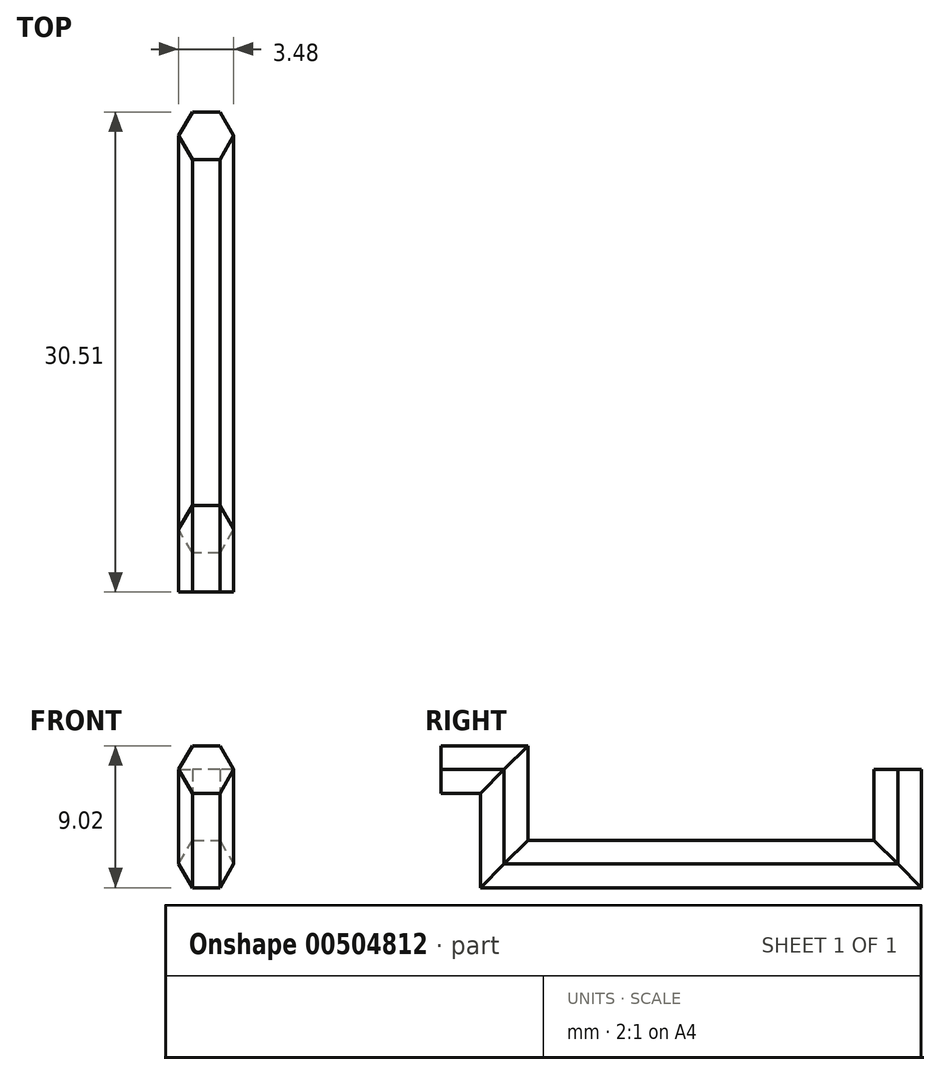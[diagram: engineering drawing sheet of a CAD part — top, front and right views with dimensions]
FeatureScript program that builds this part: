
annotation { "Feature Type Name" : "Feature", "Feature Type Description" : "" }
export const myFeature = defineFeature(function(context is Context, id is Id, definition is map)
    precondition{}
    {
        {
            var Q0;
            Q0=qCreatedBy(makeId("Right.planeOp"),FACE);
            var sketch = newSketch(context, id + "F0", { "sketchPlane" : qUnion([Q0])});
            skLineSegment(sketch, "E0", {"start": v(-12.5, 0) * mm, "end": v(12.5, 0) * mm});
            skLineSegment(sketch, "E1", {"start": v(12.5, 0) * mm, "end": v(12.5, 6) * mm});
            skLineSegment(sketch, "E2", {"start": v(-12.5, 0) * mm, "end": v(-12.5, 6) * mm});
            skLineSegment(sketch, "E3", {"start": v(-12.5, 6) * mm, "end": v(-16.5, 6) * mm});
            skLineSegment(sketch, "E4", {"start": v(-3.5, 0) * mm, "end": v(-3.5, -5) * mm});
            skPoint(sketch, "E5", {"position": v(12.5, 6) * mm});
            skPoint(sketch, "E6", {"position": v(-3.5, -5) * mm});
            skSolve(sketch);
        }
        {
            var Q0;
            Q0=qCreatedBy(makeId("Front.planeOp"),FACE);
            var sketch = newSketch(context, id + "F1", { "sketchPlane" : qUnion([Q0])});
            skCircle(sketch, "E7.cCircle", {"center": v(0, 0) * mm, "radius": 1.51 * mm, "construction": true});
            skLineSegment(sketch, "E7.0", {"start": v(0.87, -1.51) * mm, "end": v(-0.87, -1.51) * mm});
            skLineSegment(sketch, "E7.1", {"start": v(-0.87, -1.51) * mm, "end": v(-1.74, 0) * mm});
            skLineSegment(sketch, "E7.2", {"start": v(-1.74, 0) * mm, "end": v(-0.87, 1.51) * mm});
            skLineSegment(sketch, "E7.3", {"start": v(-0.87, 1.51) * mm, "end": v(0.87, 1.51) * mm});
            skLineSegment(sketch, "E7.4", {"start": v(0.87, 1.51) * mm, "end": v(1.74, 0) * mm});
            skLineSegment(sketch, "E7.5", {"start": v(1.74, 0) * mm, "end": v(0.87, -1.51) * mm});
            skPoint(sketch, "E7.0.midPoint", {"position": v(0, -1.51) * mm});
            skSolve(sketch);
        }
        {
            var Q0;
            Q0=makeQuery(id+"F1.imprint","IMPRINT",FACE,{"disambiguationData":[TD([[makeQuery(id+"F1.imprint","IMPRINT",EDGE,{"derivedFrom":sQuery(id+"F1.wireOp",EDGE,"E7.0")}),-1.0]])]});
            var Q1;
            Q1=sQuery(id+"F0.wireOp",EDGE,"E0");
            var Q2;
            Q2=sQuery(id+"F0.wireOp",EDGE,"E2");
            var Q3;
            Q3=sQuery(id+"F0.wireOp",EDGE,"E3");
            sweep(context, id + "F2", {"profiles" : qUnion([Q0]), "path" : qUnion([Q1, Q2, Q3])});
        }
        {
            var Q0;
            Q0=makeQuery(id+"F1.imprint","IMPRINT",FACE,{"disambiguationData":[TD([[makeQuery(id+"F1.imprint","IMPRINT",EDGE,{"derivedFrom":sQuery(id+"F1.wireOp",EDGE,"E7.0")}),-1.0]])]});
            var Q1;
            Q1=sQuery(id+"F0.wireOp",EDGE,"E0");
            var Q2;
            Q2=sQuery(id+"F0.wireOp",EDGE,"E1");
            sweep(context, id + "F3", {"operationType" : NewBodyOperationType.ADD, "profiles" : qUnion([Q0]), "path" : qUnion([Q1, Q2])});
        }
    });
